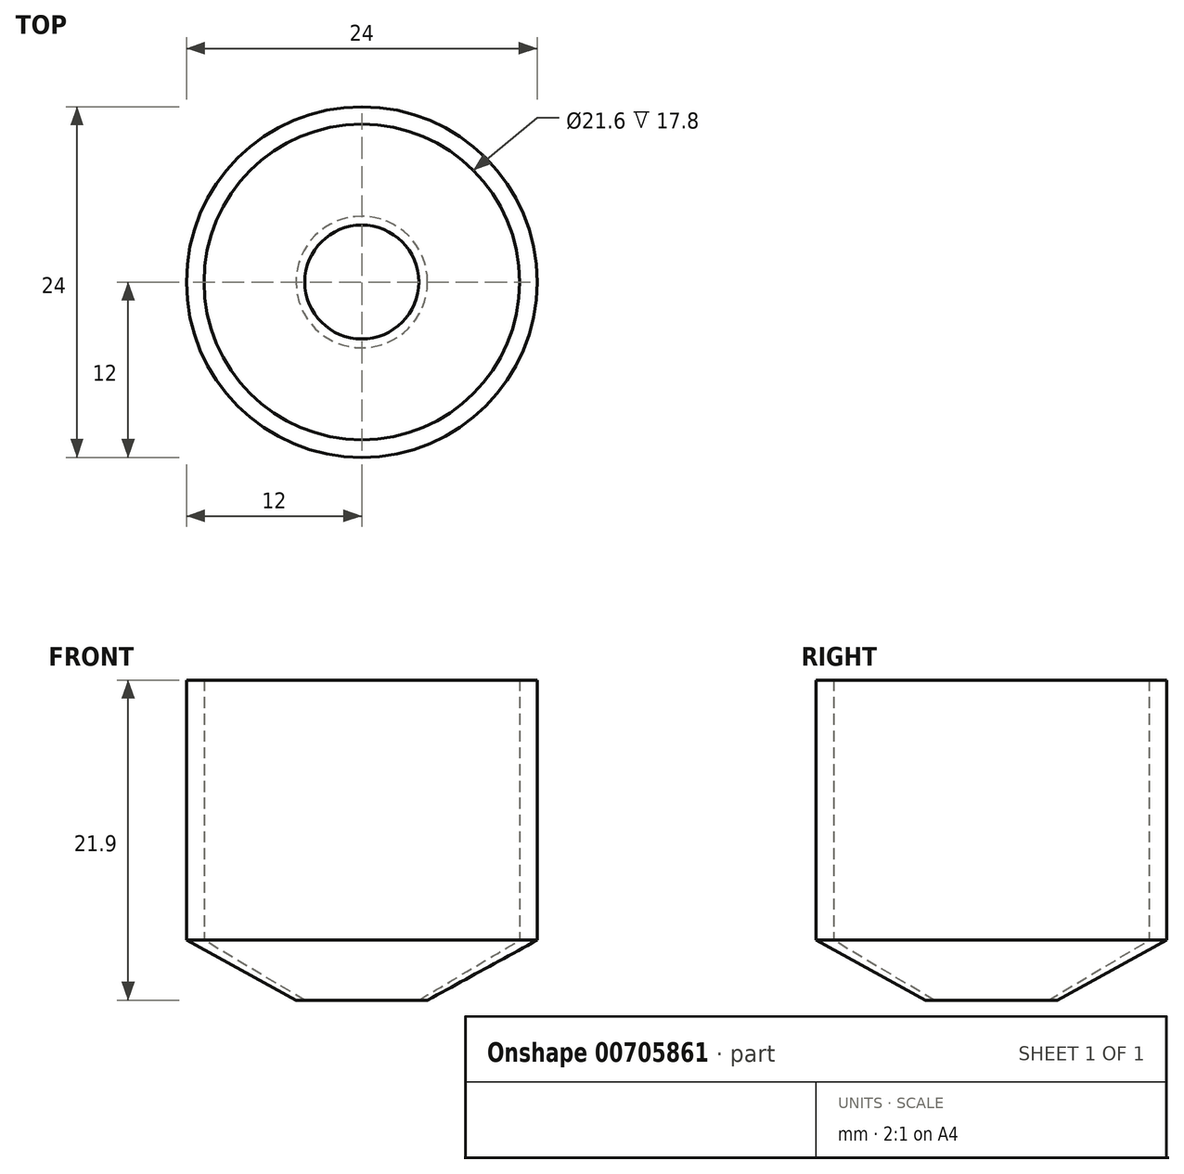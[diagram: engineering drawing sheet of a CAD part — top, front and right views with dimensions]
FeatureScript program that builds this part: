
annotation { "Feature Type Name" : "Feature", "Feature Type Description" : "" }
export const myFeature = defineFeature(function(context is Context, id is Id, definition is map)
    precondition{}
    {
        {
            var Q0;
            Q0=qCreatedBy(makeId("Top.planeOp"),FACE);
            var sketch = newSketch(context, id + "F0", { "sketchPlane" : qUnion([Q0])});
            skCircle(sketch, "E0", {"center": v(0, 0) * mm, "radius": 10.8 * mm});
            skCircle(sketch, "E1", {"center": v(0, 0) * mm, "radius": 12 * mm});
            skSolve(sketch);
        }
        {
            var Q0;
            Q0=makeQuery(id+"F0.imprint","IMPRINT",FACE,{"disambiguationData":[TD([[makeQuery(id+"F0.imprint","IMPRINT",EDGE,{"derivedFrom":sQuery(id+"F0.wireOp",EDGE,"E0")}),-1.0]])]});
            extrude(context, id + "F1", {"entities" : qUnion([Q0]), "depth" : 17.8 * mm, "offsetDistance" : 25 * mm});
        }
        {
            var Q0;
            Q0=qCreatedBy(makeId("Front.planeOp"),FACE);
            var sketch = newSketch(context, id + "F2", { "sketchPlane" : qUnion([Q0])});
            skLineSegment(sketch, "E2", {"start": v(-10.8, 0) * mm, "end": v(-12, 0) * mm});
            skPoint(sketch, "E3", {"position": v(0, -4.1) * mm});
            skPoint(sketch, "E4", {"position": v(-3.9, -4.1) * mm});
            skPoint(sketch, "E5", {"position": v(-4.5, -4.1) * mm});
            skLineSegment(sketch, "E6", {"start": v(-12, 0) * mm, "end": v(-4.5, -4.1) * mm});
            skLineSegment(sketch, "E7", {"start": v(-3.9, -4.1) * mm, "end": v(-4.5, -4.1) * mm});
            skLineSegment(sketch, "E8", {"start": v(-3.9, -4.1) * mm, "end": v(-10.8, 0) * mm});
            skLineSegment(sketch, "E9", {"start": v(0, 0) * mm, "end": v(0, -4.1) * mm});
            skPoint(sketch, "E10", {"position": v(6.37, -16.85) * mm});
            skPoint(sketch, "E11", {"position": v(-23.03, -14.33) * mm});
            skPoint(sketch, "E12", {"position": v(-39.02, -8.19) * mm});
            skSolve(sketch);
        }
        {
            var Q0;
            Q0 = qSketchRegion(id + "F2", true);
            var Q1;
            Q1=sQuery(id+"F2.wireOp",EDGE,"E9");
            revolve(context, id + "F3", {"operationType" : NewBodyOperationType.ADD, "surfaceOperationType" : NewSurfaceOperationType.NEW, "entities" : qUnion([Q0]), "axis" : qUnion([Q1]), "revolveType" : RevolveType.FULL});
        }
    });
